# Revit family: Seating-Casual-Naughtone-Pinch_Low_Stool
name_source: partatom
category: Furniture
revit_build: Autodesk Revit 2014 (Build: 20130709_2115(x64)
units: mm (PartAtom-declared; Revit-internal decimal feet)

## types (1)
- Pinch Low Stool
    AssetIdentifier = PIN-LO
    Barcode = 0
    COBie Description = The Award winning Pinch stool is another classic in the naughtone range and a truly versatile product. The fully upholstered form of the Pinch stool offers a comfortable seat, whether used at a table or mingled with soft seating. It can be sat on or straddled and the pinch stool has no obvious direction so lends itself to being scattered in a space. Use the Pinch stool as functional occasional seating and to add life to any interior space.
    Cost = 0 $
    Current Revision = 1
    Depth = 450 mm  [stored 1.47638 ft]
    Description = Multifunctional Upholstered Low Stool
    Height = 400 mm  [stored 1.31234 ft]
    Length = 600 mm
    Manufacturer = Naughtone
    Model = Pinch
    Name = Furniture -Seating-Casual-Naughtone-Pinch_Low_Stool
    Option = Low Stool
    Product Code = PIN-LO
    Product URL = http://www.naughtone.com
    Seat Height = 350 mm  [stored 1.14829 ft]
    SerialNumber = 0
    TagNumber = 0
    TypeName = 600mmx450mmx400mm - Multifunctional Upholstered Stool
    URL = http://www.naughtone.com
    Uniclass = Pr_40_50_12
    WarrantyDuration = 60

note: [stored X ft] marks values corroborated as IEEE doubles in the binary element streams (Revit-internal decimal feet)

## geometry (parser evidence)
native form markers: Sweep x3
no freeform markers — native parametric forms only
